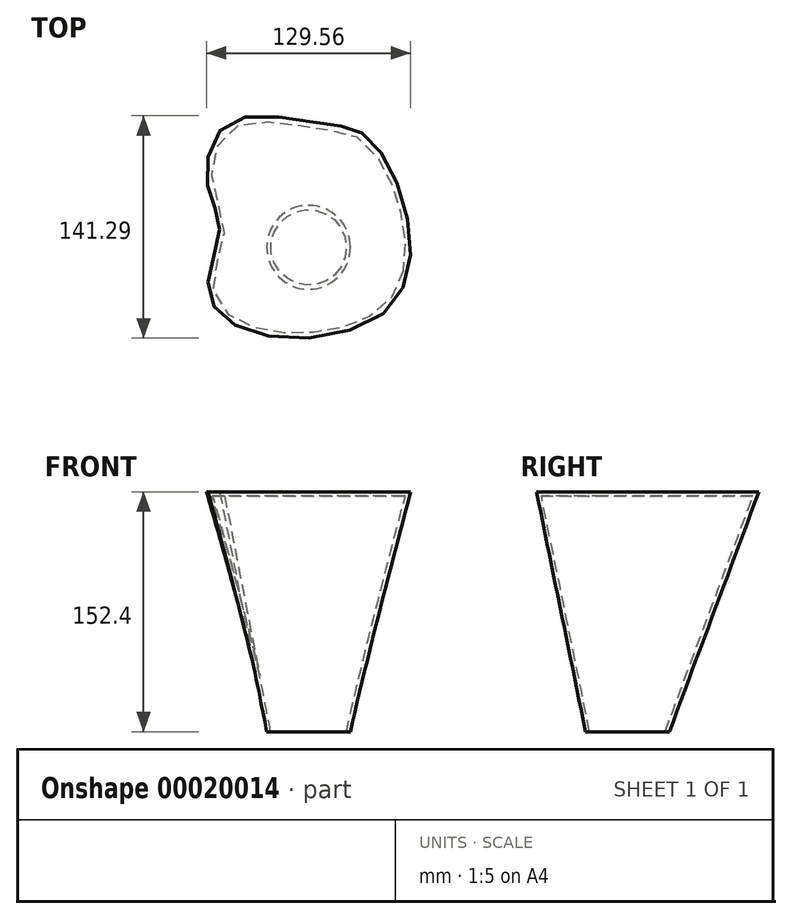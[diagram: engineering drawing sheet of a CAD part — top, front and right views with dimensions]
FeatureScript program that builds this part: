
annotation { "Feature Type Name" : "Feature", "Feature Type Description" : "" }
export const myFeature = defineFeature(function(context is Context, id is Id, definition is map)
    precondition{}
    {
        {
            var Q0;
            Q0=qCreatedBy(makeId("Top.planeOp"),FACE);
            var sketch = newSketch(context, id + "F0", { "sketchPlane" : qUnion([Q0])});
            skCircle(sketch, "E0", {"center": v(0, 0) * mm, "radius": 26.6 * mm});
            skSolve(sketch);
        }
        {
            var Q0;
            Q0=qCreatedBy(makeId("Top.planeOp"),FACE);
            cPlane(context, id + "F1", {"entities" : qUnion([Q0]), "cplaneType" : CPlaneType.OFFSET, "offset" : 152.4 * mm, "width" : 152.4 * mm, "height" : 152.4 * mm});
        }
        {
            var Q0;
            Q0=qCreatedBy(id+"F1.planeOp",FACE);
            var sketch = newSketch(context, id + "F2", { "sketchPlane" : qUnion([Q0])});
            skFitSpline(sketch, "E1", {"points": [v(-64.11, 39.18) * mm, v(-51.24, 78.64) * mm, v(6.73, 79.06) * mm, v(37.58, 69.83) * mm, v(63.6, 13.08) * mm, v(47.45, -42) * mm, v(-33.64, -54.61) * mm, v(-63.84, -26.7) * mm, v(-56.45, 11.66) * mm, v(-64.11, 39.18) * mm]});
            skSolve(sketch);
        }
        {
            var Q0;
            Q0=makeQuery(id+"F2.imprint","IMPRINT",FACE,{"disambiguationData":[TD([[makeQuery(id+"F2.imprint","IMPRINT",EDGE,{"derivedFrom":sQuery(id+"F2.wireOp",EDGE,"E1")}),-1.0]])]});
            var Q1;
            Q1=makeQuery(id+"F0.imprint","IMPRINT",FACE,{"disambiguationData":[TD([[makeQuery(id+"F0.imprint","IMPRINT",EDGE,{"derivedFrom":sQuery(id+"F0.wireOp",EDGE,"E0")}),1.0]])]});
            loft(context, id + "F3", {"sheetProfilesArray" : [{ "sheetProfileEntities" : qUnion([Q0]) }, { "sheetProfileEntities" : qUnion([Q1]) }]});
        }
        {
            var Q0;
            Q0=makeQuery(id+"F3.opLoft","CAP_FACE",FACE,{"disambiguationData":[OSD([makeQuery(id+"F0.imprint","IMPRINT",FACE,{"disambiguationData":[TD([[makeQuery(id+"F0.imprint","IMPRINT",EDGE,{"derivedFrom":sQuery(id+"F0.wireOp",EDGE,"E0")}),1.0]])]})])],"isStart":true});
            shell(context, id + "F4", {"entities" : qUnion([Q0]), "thickness" : 2.54 * mm});
        }
    });
